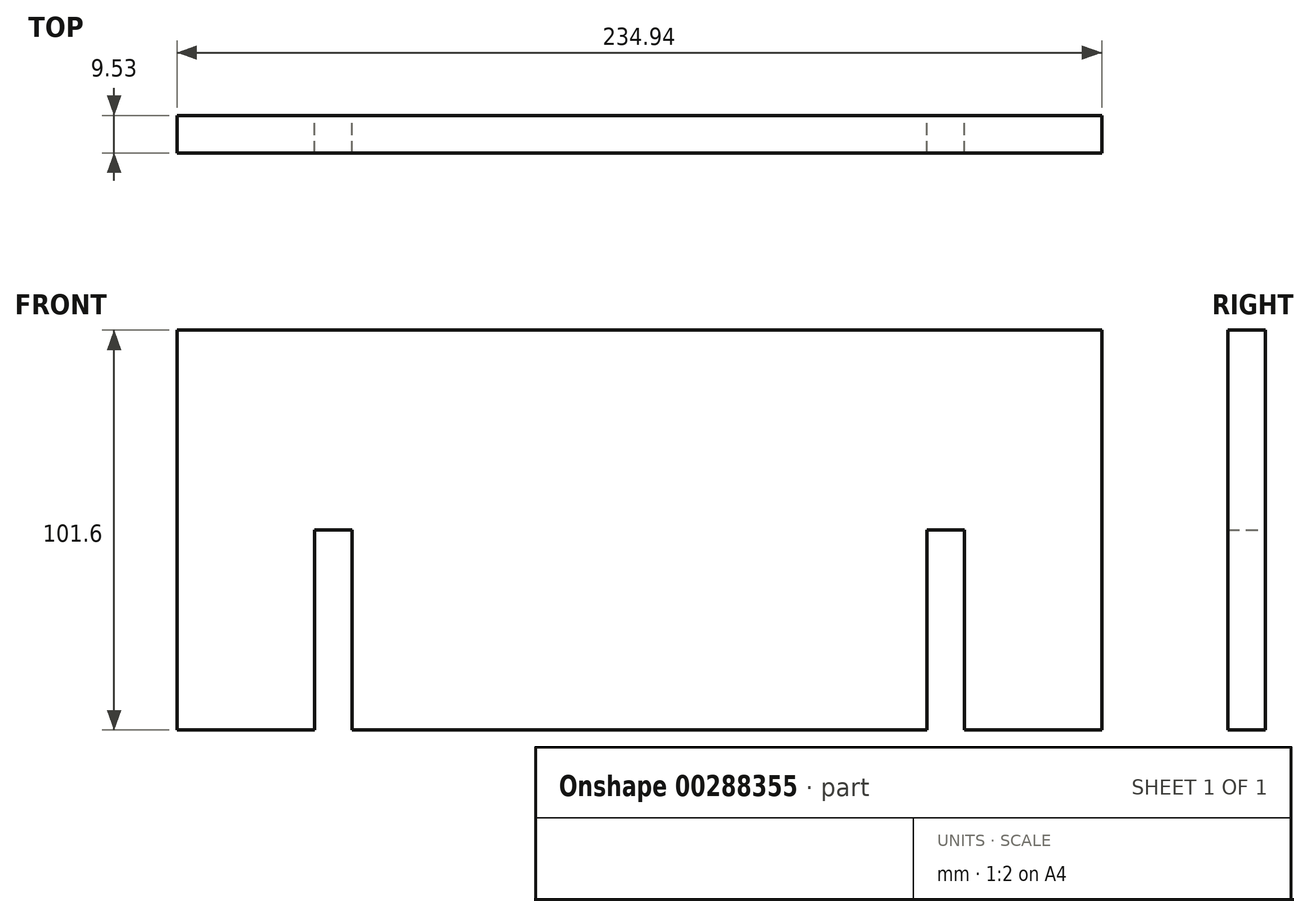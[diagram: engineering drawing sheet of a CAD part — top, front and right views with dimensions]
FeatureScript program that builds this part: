
annotation { "Feature Type Name" : "Feature", "Feature Type Description" : "" }
export const myFeature = defineFeature(function(context is Context, id is Id, definition is map)
    precondition{}
    {
        {
            var Q0;
            Q0=qCreatedBy(makeId("Front.planeOp"),FACE);
            var sketch = newSketch(context, id + "F0", { "sketchPlane" : qUnion([Q0])});
            skLineSegment(sketch, "E0.bottom", {"start": v(-117.48, -50.8) * mm, "end": v(-82.55, -50.8) * mm});
            skLineSegment(sketch, "E0.top", {"start": v(-117.48, 50.8) * mm, "end": v(117.48, 50.8) * mm});
            skLineSegment(sketch, "E0.left", {"start": v(-117.48, -50.8) * mm, "end": v(-117.48, 50.8) * mm});
            skLineSegment(sketch, "E0.right", {"start": v(117.48, -50.8) * mm, "end": v(117.48, 50.8) * mm});
            skPoint(sketch, "E0.middle", {"position": v(0, 0) * mm});
            skLineSegment(sketch, "E1.top", {"start": v(-82.55, 0) * mm, "end": v(-73.03, 0) * mm});
            skLineSegment(sketch, "E1.left", {"start": v(-82.55, -50.8) * mm, "end": v(-82.55, 0) * mm});
            skLineSegment(sketch, "E1.right", {"start": v(-73.03, -50.8) * mm, "end": v(-73.03, 0) * mm});
            skLineSegment(sketch, "E2.trimOffspring", {"start": v(-73.03, -50.8) * mm, "end": v(73.02, -50.8) * mm});
            skLineSegment(sketch, "E3.top", {"start": v(82.55, 0) * mm, "end": v(73.03, 0) * mm});
            skLineSegment(sketch, "E3.left", {"start": v(82.55, -50.8) * mm, "end": v(82.55, 0) * mm});
            skLineSegment(sketch, "E3.right", {"start": v(73.03, -50.8) * mm, "end": v(73.03, 0) * mm});
            skLineSegment(sketch, "E4.trimOffspring", {"start": v(82.55, -50.8) * mm, "end": v(117.48, -50.8) * mm});
            skSolve(sketch);
        }
        {
            var Q0;
            Q0 = qSketchRegion(id + "F0", true);
            extrude(context, id + "F1", {"entities" : qUnion([Q0]), "depth" : 9.52 * mm});
        }
    });
